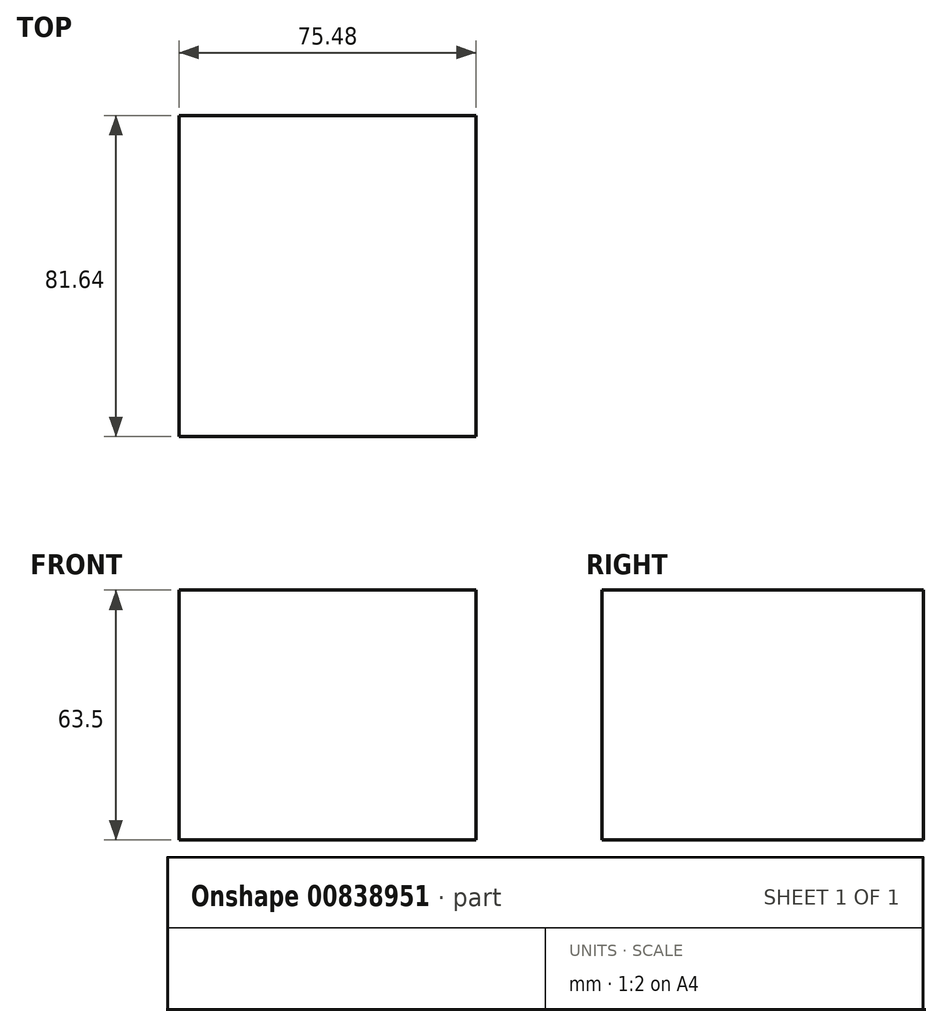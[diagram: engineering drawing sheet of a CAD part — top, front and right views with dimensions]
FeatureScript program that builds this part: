
annotation { "Feature Type Name" : "Feature", "Feature Type Description" : "" }
export const myFeature = defineFeature(function(context is Context, id is Id, definition is map)
    precondition{}
    {
        {
            var Q0;
            Q0=qCreatedBy(makeId("Top.planeOp"),FACE);
            var sketch = newSketch(context, id + "F0", { "sketchPlane" : qUnion([Q0])});
            skLineSegment(sketch, "E0.bottom", {"start": v(-157.32, 0) * mm, "end": v(-81.84, 0) * mm});
            skLineSegment(sketch, "E0.top", {"start": v(-157.32, -81.64) * mm, "end": v(-81.84, -81.64) * mm});
            skLineSegment(sketch, "E0.left", {"start": v(-157.32, 0) * mm, "end": v(-157.32, -81.64) * mm});
            skLineSegment(sketch, "E0.right", {"start": v(-81.84, 0) * mm, "end": v(-81.84, -81.64) * mm});
            skSolve(sketch);
        }
        {
            var Q0;
            Q0=makeQuery(id+"F0.imprint","IMPRINT",FACE,{"disambiguationData":[TD([[makeQuery(id+"F0.imprint","IMPRINT",EDGE,{"derivedFrom":sQuery(id+"F0.wireOp",EDGE,"E0.bottom")}),-1.0]])]});
            extrude(context, id + "F1", {"entities" : qUnion([Q0]), "depth" : 63.5 * mm, "offsetDistance" : 25.4 * mm});
        }
    });
